# Revit family: AR
name_source: partatom
category: Lighting Fixtures
units: mm (PartAtom-declared; Revit-internal decimal feet)

## family parameters
Always vertical = Yes
Cut with Voids When Loaded = No
Light Source = Yes
OmniClass Number = 23.80.70.14.21
OmniClass Title = Street and Roadway Lighting
Part Type = Normal
Room Calculation Point = No
Round Connector Dimension = Use Diameter
Shared = No
Work Plane-Based = No

## types (1)
- AR
    Apparent Load = 0 VA
    Assembly Code = D5020200
    Color Filter = 16777215
    Default Elevation = 0"
    Description = Site/Roadway Luminare
    Dimming Lamp Color Temperature Shift = <None>
    Emit Shape Visible in Rendering = No
    Emit from Rectangle Length = 14"
    Emit from Rectangle Width = 14"
    Finish = All colors shall be a Super TGIC thermoset polyester powder coat paint
    Full Load Current = 0 A
    Glass Material = Glass
    Housing material = Powdercoat - Black
    Initial Lumens = 40000 lm
    LED Driver = Powdercoat -  Graphite
    Lamp = LED
    Manufacturer = Kim Lighting
    MasterFormat Number = 26 56 16, 26 56 19, 26 56 29
    MasterFormat Title = Parking Lighting, Roadway Lighting, Site Lighting
    Model = The Archetype® Large PicoPrism LED
    Note Text = LF
    Note Visible = No
    Number of Poles = 1
    OmniClass Number = 23-80 70 14 21
    OmniClass Title = Street and Roadway Lighting
    Photometric Notes = More IES files download on Photometric Web Link
    Photometric Web File = ar1p35-80l4k.IES
    Pole Visible = Yes
    Power Factor = 1
    Series = The Archetype
    Tilt Angle = 60.00°
    Total Pole Height = 180"
    Type Comments = Lighting Fixture
    URL = https://www.currentlighting.com
    Voltage = 240 V
    Wattage Comments = 95W & 188W

## geometry (parser evidence)
native form markers: Blend x4, Sweep x5
no freeform markers — native parametric forms only
